# Revit family: DLB070013
name_source: partatom
category: Modèles génériques
revit_build: Autodesk Revit 2015 (Build: 20140606_1530(x64)
units: mm (PartAtom-declared; Revit-internal decimal feet)

## types (1)
- Type 1
    Category = WC
    Commentaires du type = Close coupled WC
    Description = French manufacturer Delabie is a leader in the European sanitary ware market for non-domestic places. Water controls, solutions for disabled people, sanitary ware, for schools, leisure centres, offices, hospitals, airports…
    Fabricant = DELABIE
    Features  = Floor-standing WC pan with dual flush cistern 3/6 L.
Bacteriostatic 304 stainless steel. Stainless steel thickness: 1.5mm.
One-piece pressed WC bowl, seam-free for better hygiene.
WC bowl surface is polished with rounded edges for easy cleaning.
Concealed perimetral flushing rim. Water supply can be recessed from below or exposed from the side (right/left).
Recessed horizontal or vertical waste outlet. Supplied with PVC pipe.
Pre-drilled holes for fixing the toilet seat. Supplied with stainless steel blanking caps when installed without toilet seat lid.
Quick and easy to install: 2 access panels with theft prevention TORX security screws.
CE marked. Complies with European standard EN 997 for 4L flush.
Optional toilet seat with or without lid.
Weight: 21kg.
    Finish = Polished satin
    Grade = CE
    ManufacturerName = DELABIE
    ManufacturerURL = http://www.delabie.com
    Material = 304 stainless steel
    ModelNumber = 110390
    Modèle = MONOBLOCO S21 WC pan
    Name = MONOBLOCO S21 WC pan
    NominalHeight = 815 mm  [stored 2.67388 ft]
    NominalLength = 370 mm  [stored 1.21391 ft]
    NominalWidth = 620 mm  [stored 2.03412 ft]
    ProductInformation = http://www.delabie.com
    Radius = 8 mm  [stored 0.0262467 ft]
    Radius Evacuartion = 50 mm  [stored 0.164042 ft]
    SerialNumber = 3456330153522
    URL = http://www.delabie.com
    Version = v1
    WarrantyDescription = Any manufacturing defect
    WarrantyDurationUnit = 10 years
    Weight = 21kg

note: [stored X ft] marks values corroborated as IEEE doubles in the binary element streams (Revit-internal decimal feet)

## geometry (parser evidence)
native form markers: Blend x14, Sweep x5
no freeform markers — native parametric forms only
